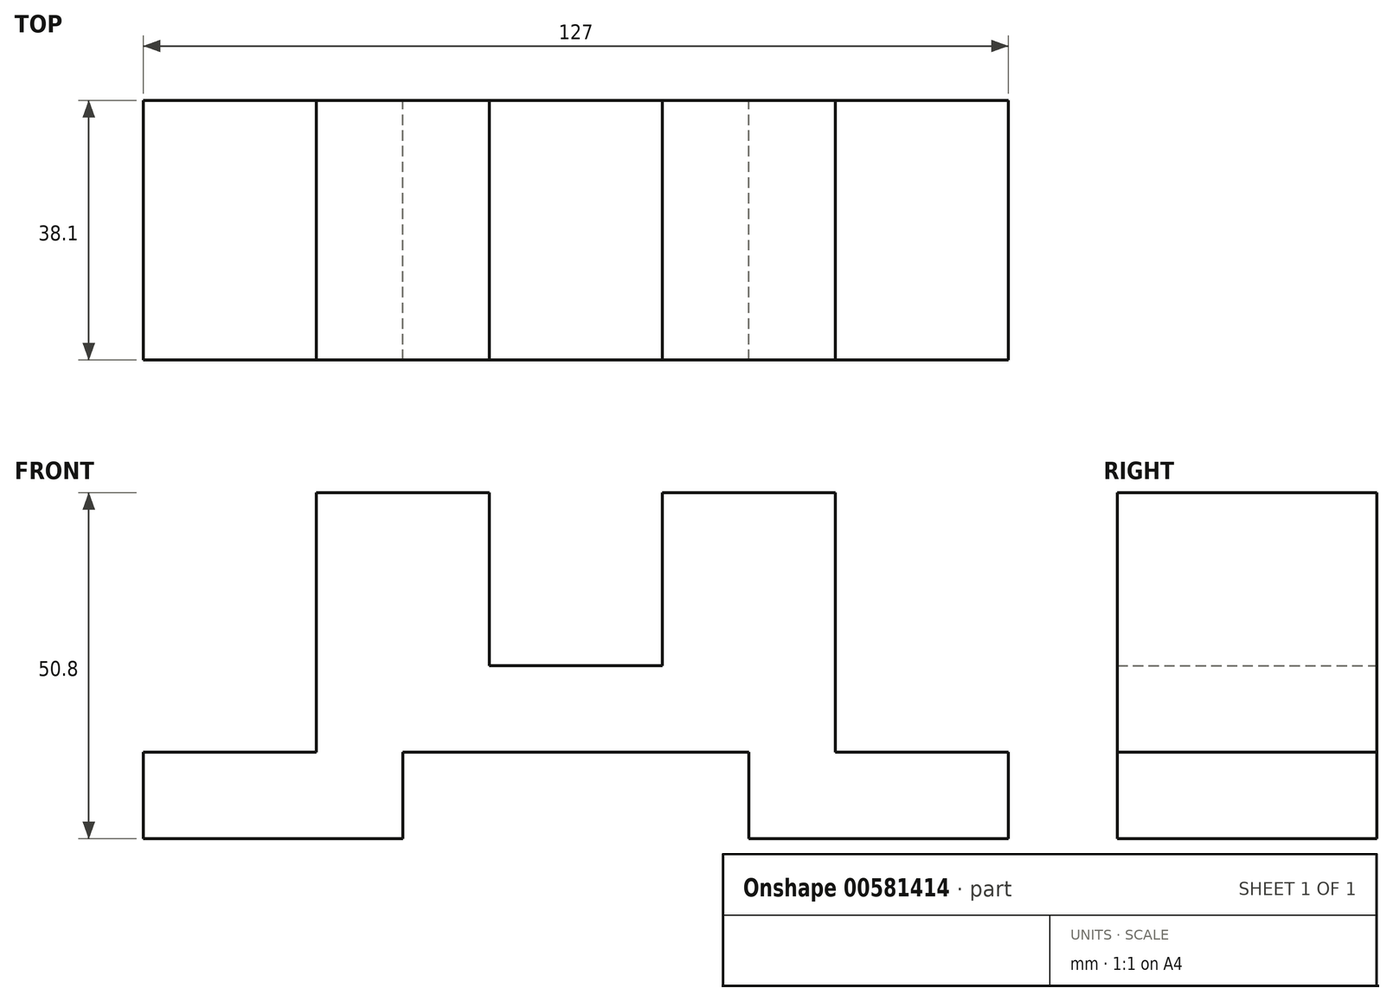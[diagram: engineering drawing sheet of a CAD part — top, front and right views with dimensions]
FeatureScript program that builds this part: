
annotation { "Feature Type Name" : "Feature", "Feature Type Description" : "" }
export const myFeature = defineFeature(function(context is Context, id is Id, definition is map)
    precondition{}
    {
        {
            var Q0;
            Q0=qCreatedBy(makeId("Front.planeOp"),FACE);
            var sketch = newSketch(context, id + "F0", { "sketchPlane" : qUnion([Q0])});
            skLineSegment(sketch, "E0", {"start": v(-60.3, -31.73) * mm, "end": v(-22.2, -31.73) * mm});
            skLineSegment(sketch, "E1", {"start": v(-22.2, -31.73) * mm, "end": v(-22.2, -19.03) * mm});
            skLineSegment(sketch, "E2", {"start": v(-22.2, -19.03) * mm, "end": v(28.6, -19.03) * mm});
            skLineSegment(sketch, "E3", {"start": v(28.6, -19.03) * mm, "end": v(28.6, -31.73) * mm});
            skLineSegment(sketch, "E4", {"start": v(28.6, -31.73) * mm, "end": v(66.7, -31.73) * mm});
            skLineSegment(sketch, "E5", {"start": v(66.7, -31.73) * mm, "end": v(66.7, -19.03) * mm});
            skLineSegment(sketch, "E6", {"start": v(66.7, -19.03) * mm, "end": v(41.3, -19.03) * mm});
            skLineSegment(sketch, "E7", {"start": v(41.3, -19.03) * mm, "end": v(41.3, 19.07) * mm});
            skLineSegment(sketch, "E8", {"start": v(41.3, 19.07) * mm, "end": v(15.9, 19.07) * mm});
            skLineSegment(sketch, "E9", {"start": v(15.9, 19.07) * mm, "end": v(15.9, -6.33) * mm});
            skLineSegment(sketch, "E10", {"start": v(15.9, -6.33) * mm, "end": v(-9.5, -6.33) * mm});
            skLineSegment(sketch, "E11", {"start": v(-9.5, -6.33) * mm, "end": v(-9.5, 19.07) * mm});
            skLineSegment(sketch, "E12", {"start": v(-9.5, 19.07) * mm, "end": v(-34.9, 19.07) * mm});
            skLineSegment(sketch, "E13", {"start": v(-34.9, 19.07) * mm, "end": v(-34.9, -19.03) * mm});
            skLineSegment(sketch, "E14", {"start": v(-34.9, -19.03) * mm, "end": v(-60.3, -19.03) * mm});
            skLineSegment(sketch, "E15", {"start": v(-60.3, -19.03) * mm, "end": v(-60.3, -31.73) * mm});
            skSolve(sketch);
        }
        {
            var Q0;
            Q0=makeQuery(id+"F0.imprint","IMPRINT",FACE,{"disambiguationData":[TD([[makeQuery(id+"F0.imprint","IMPRINT",EDGE,{"derivedFrom":sQuery(id+"F0.wireOp",EDGE,"E0")}),1.0]])]});
            extrude(context, id + "F1", {"entities" : qUnion([Q0]), "depth" : 38.1 * mm, "offsetDistance" : 25.4 * mm});
        }
    });
